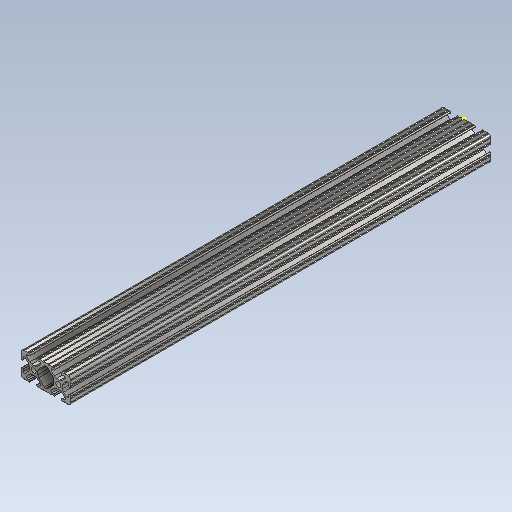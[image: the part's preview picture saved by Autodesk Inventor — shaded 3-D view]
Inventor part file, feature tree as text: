
AUTODESK INVENTOR PART (.ipt)
format: ipt  version: 2020 (Build 240168000, 168)  size: 353,280 bytes
history: native  units: in
note: dims shown in document units (in); Inventor stores cm internally (conversion verified against a paired STEP export)
features: sketch x2, extrude x1
ambient origin geometry x8: Origin, YZ Plane, XZ Plane, XY Plane, X Axis, Y Axis, Z Axis, Center Point
bodies: Solid1 (feature_tree)
feature tree (3):
  extrude  "Extrusion1"  [1 undecoded]
  sketch  "Sketch2"
  sketch  "Sketch1"  dims[d0=17.0in d1=0.0in]
note: 1 required parameter value undecoded (feature->parameter linkage not recoverable at this tier; creation-order binding heuristic only, values carry confidence <= 0.55)
